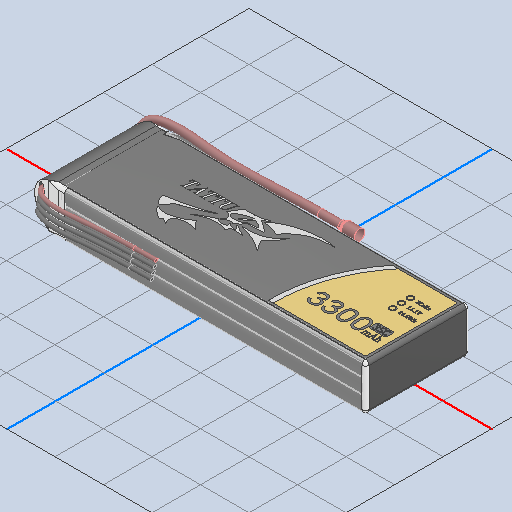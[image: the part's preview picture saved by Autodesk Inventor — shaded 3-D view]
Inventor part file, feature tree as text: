
AUTODESK INVENTOR PART (.ipt)
format: ipt  version: 2022 (Build 260153000, 153)  size: 1,471,488 bytes
history: mixed  units: mm
features: other x14, revolve x2, mirror x1, fillet x1, imported_body x1
ambient origin geometry x8: Origin, YZ Plane, XZ Plane, XY Plane, X Axis, Y Axis, Z Axis, Center Point
bodies: Body1 (imported_parasolid), Body2 (imported_parasolid), Body3 (imported_parasolid), Body4 (imported_parasolid), Body5 (imported_parasolid), Body6 (imported_parasolid), Body7 (imported_parasolid), Body8 (imported_parasolid), Body9 (imported_parasolid)
feature tree (19):
  other  "Твердое тело1"
  other  "Твердое тело2"
  other  "Твердое тело3"
  other  "Твердое тело4"
  other  "Твердое тело5"
  other  "Твердое тело6"
  other  "Твердое тело7"
  other  "Твердое тело8"
  other  "Твердое тело9"
  mirror  "Mirror1"
  fillet  "Redondeo8"  [1 undecoded]
  other  "Cortar-Extruir8"
  other  "Barrer5[1]"
  other  "Barrer5[2]"
  other  "Barrer5[3]"
  other  "Barrer5[4]"
  revolve  "Revolución3"  [1 undecoded]
  revolve  "Revolución4"  [1 undecoded]
  imported_body  NMx_Import_Brep_tag  [imported B-rep: ~22 faces, bbox_mm=None]
note: 3 required parameter values undecoded (feature->parameter linkage not recoverable at this tier; creation-order binding heuristic only, values carry confidence <= 0.55)
